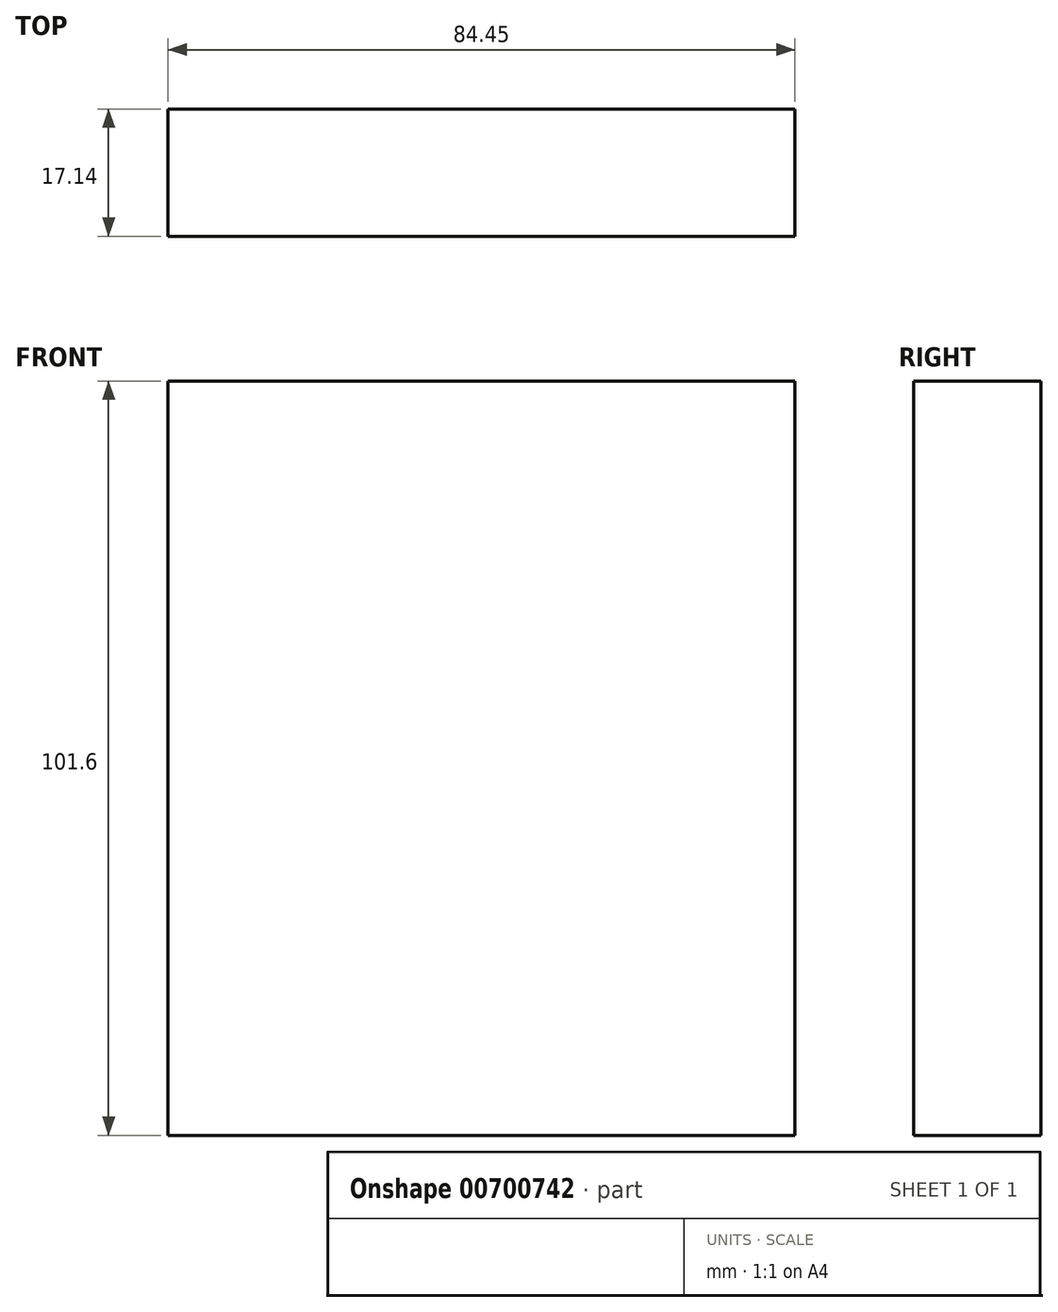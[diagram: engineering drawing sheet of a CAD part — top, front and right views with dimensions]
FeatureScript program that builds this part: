
annotation { "Feature Type Name" : "Feature", "Feature Type Description" : "" }
export const myFeature = defineFeature(function(context is Context, id is Id, definition is map)
    precondition{}
    {
        {
            var Q0;
            Q0=qCreatedBy(makeId("Front.planeOp"),FACE);
            var sketch = newSketch(context, id + "F0", { "sketchPlane" : qUnion([Q0])});
            skLineSegment(sketch, "E0.bottom", {"start": v(0, 0) * mm, "end": v(84.46, 0) * mm});
            skLineSegment(sketch, "E0.top", {"start": v(0, 101.6) * mm, "end": v(84.46, 101.6) * mm});
            skLineSegment(sketch, "E0.left", {"start": v(0, 0) * mm, "end": v(0, 101.6) * mm});
            skLineSegment(sketch, "E0.right", {"start": v(84.46, 0) * mm, "end": v(84.46, 101.6) * mm});
            skSolve(sketch);
        }
        {
            var Q0;
            Q0 = qSketchRegion(id + "F0", true);
            extrude(context, id + "F1", {"entities" : qUnion([Q0]), "depth" : 17.14 * mm, "offsetDistance" : 25.4 * mm});
        }
    });
